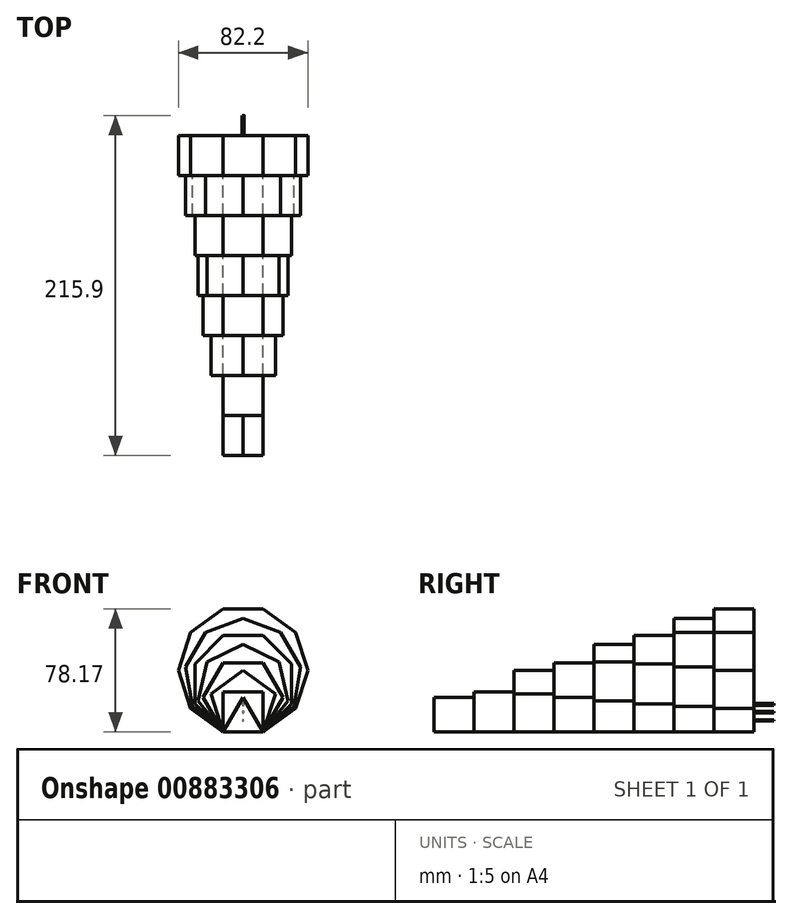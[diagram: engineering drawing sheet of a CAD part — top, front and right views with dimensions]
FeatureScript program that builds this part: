
annotation { "Feature Type Name" : "Feature", "Feature Type Description" : "" }
export const myFeature = defineFeature(function(context is Context, id is Id, definition is map)
    precondition{}
    {
        {
            var Q0;
            Q0=qCreatedBy(makeId("Front.planeOp"),FACE);
            var sketch = newSketch(context, id + "F0", { "sketchPlane" : qUnion([Q0])});
            skCircle(sketch, "E0.cCircle", {"center": v(0, 0) * mm, "radius": 14.66 * mm, "construction": true});
            skLineSegment(sketch, "E0.0", {"start": v(12.7, -7.33) * mm, "end": v(-12.7, -7.33) * mm});
            skLineSegment(sketch, "E0.1", {"start": v(-12.7, -7.33) * mm, "end": v(0, 14.66) * mm});
            skLineSegment(sketch, "E0.2", {"start": v(0, 14.66) * mm, "end": v(12.7, -7.33) * mm});
            skSolve(sketch);
        }
        {
            var Q0;
            Q0=makeQuery(id+"F0.imprint","IMPRINT",FACE,{"disambiguationData":[TD([[makeQuery(id+"F0.imprint","IMPRINT",EDGE,{"derivedFrom":sQuery(id+"F0.wireOp",EDGE,"E0.0")}),-1.0]])]});
            var Q1;
            Q1 = qSketchRegion(id + "F0", true);
            extrude(context, id + "F1", {"entities" : qUnion([Q0, Q1]), "depth" : 203.2 * mm, "offsetDistance" : 25.4 * mm});
        }
        {
            var Q0;
            Q0=qCreatedBy(makeId("Front.planeOp"),FACE);
            var sketch = newSketch(context, id + "F2", { "sketchPlane" : qUnion([Q0])});
            skCircle(sketch, "E1.cCircle", {"center": v(0, 5.37) * mm, "radius": 17.96 * mm, "construction": true});
            skLineSegment(sketch, "E1.0", {"start": v(12.7, -7.33) * mm, "end": v(-12.7, -7.33) * mm});
            skLineSegment(sketch, "E1.1", {"start": v(-12.7, -7.33) * mm, "end": v(-12.7, 18.07) * mm});
            skLineSegment(sketch, "E1.2", {"start": v(-12.7, 18.07) * mm, "end": v(12.7, 18.07) * mm});
            skLineSegment(sketch, "E1.3", {"start": v(12.7, 18.07) * mm, "end": v(12.7, -7.33) * mm});
            skSolve(sketch);
        }
        {
            var Q0;
            Q0 = qSketchRegion(id + "F2", true);
            extrude(context, id + "F3", {"entities" : qUnion([Q0]), "operationType" : NewBodyOperationType.ADD, "depth" : 177.8 * mm, "offsetDistance" : 25.4 * mm});
        }
        {
            var Q0;
            Q0=qCreatedBy(makeId("Front.planeOp"),FACE);
            var sketch = newSketch(context, id + "F4", { "sketchPlane" : qUnion([Q0])});
            skCircle(sketch, "E2.cCircle", {"center": v(0, 10.15) * mm, "radius": 21.6 * mm, "construction": true});
            skLineSegment(sketch, "E2.0", {"start": v(12.7, -7.33) * mm, "end": v(-12.7, -7.33) * mm});
            skLineSegment(sketch, "E2.1", {"start": v(-12.7, -7.33) * mm, "end": v(-20.55, 16.82) * mm});
            skLineSegment(sketch, "E2.2", {"start": v(-20.55, 16.82) * mm, "end": v(0, 31.75) * mm});
            skLineSegment(sketch, "E2.3", {"start": v(0, 31.75) * mm, "end": v(20.55, 16.82) * mm});
            skLineSegment(sketch, "E2.4", {"start": v(20.55, 16.82) * mm, "end": v(12.7, -7.33) * mm});
            skSolve(sketch);
        }
        {
            var Q0;
            Q0 = qSketchRegion(id + "F4", true);
            extrude(context, id + "F5", {"entities" : qUnion([Q0]), "operationType" : NewBodyOperationType.ADD, "depth" : 152.4 * mm, "offsetDistance" : 25.4 * mm});
        }
        {
            var Q0;
            Q0=qCreatedBy(makeId("Front.planeOp"),FACE);
            var sketch = newSketch(context, id + "F6", { "sketchPlane" : qUnion([Q0])});
            skCircle(sketch, "E3.cCircle", {"center": v(0, 14.66) * mm, "radius": 25.4 * mm, "construction": true});
            skLineSegment(sketch, "E3.0", {"start": v(12.7, -7.33) * mm, "end": v(-12.7, -7.33) * mm});
            skLineSegment(sketch, "E3.1", {"start": v(-12.7, -7.33) * mm, "end": v(-25.4, 14.66) * mm});
            skLineSegment(sketch, "E3.2", {"start": v(-25.4, 14.66) * mm, "end": v(-12.7, 36.66) * mm});
            skLineSegment(sketch, "E3.3", {"start": v(-12.7, 36.66) * mm, "end": v(12.7, 36.66) * mm});
            skLineSegment(sketch, "E3.4", {"start": v(12.7, 36.66) * mm, "end": v(25.4, 14.66) * mm});
            skLineSegment(sketch, "E3.5", {"start": v(25.4, 14.66) * mm, "end": v(12.7, -7.33) * mm});
            skSolve(sketch);
        }
        {
            var Q0;
            Q0 = qSketchRegion(id + "F6", true);
            extrude(context, id + "F7", {"entities" : qUnion([Q0]), "operationType" : NewBodyOperationType.ADD, "depth" : 127 * mm, "offsetDistance" : 25.4 * mm});
        }
        {
            var Q0;
            Q0=qCreatedBy(makeId("Front.planeOp"),FACE);
            var sketch = newSketch(context, id + "F8", { "sketchPlane" : qUnion([Q0])});
            skCircle(sketch, "E4.cCircle", {"center": v(0, 19.04) * mm, "radius": 29.27 * mm, "construction": true});
            skLineSegment(sketch, "E4.0", {"start": v(12.7, -7.33) * mm, "end": v(-12.7, -7.33) * mm});
            skLineSegment(sketch, "E4.1", {"start": v(-12.7, -7.33) * mm, "end": v(-28.54, 12.53) * mm});
            skLineSegment(sketch, "E4.2", {"start": v(-28.54, 12.53) * mm, "end": v(-22.88, 37.29) * mm});
            skLineSegment(sketch, "E4.3", {"start": v(-22.88, 37.29) * mm, "end": v(0, 48.3) * mm});
            skLineSegment(sketch, "E4.4", {"start": v(0, 48.3) * mm, "end": v(22.88, 37.29) * mm});
            skLineSegment(sketch, "E4.5", {"start": v(22.88, 37.29) * mm, "end": v(28.54, 12.53) * mm});
            skLineSegment(sketch, "E4.6", {"start": v(28.54, 12.53) * mm, "end": v(12.7, -7.33) * mm});
            skSolve(sketch);
        }
        {
            var Q0;
            Q0=makeQuery(id+"F8.imprint","IMPRINT",FACE,{"disambiguationData":[TD([[makeQuery(id+"F8.imprint","IMPRINT",EDGE,{"derivedFrom":sQuery(id+"F8.wireOp",EDGE,"E4.0")}),-1.0]])]});
            var Q1;
            Q1 = qSketchRegion(id + "F8", true);
            extrude(context, id + "F9", {"entities" : qUnion([Q0, Q1]), "operationType" : NewBodyOperationType.ADD, "depth" : 101.6 * mm, "offsetDistance" : 25.4 * mm});
        }
        {
            var Q0;
            Q0=qCreatedBy(makeId("Front.planeOp"),FACE);
            var sketch = newSketch(context, id + "F10", { "sketchPlane" : qUnion([Q0])});
            skCircle(sketch, "E5.cCircle", {"center": v(0, 23.33) * mm, "radius": 33.19 * mm, "construction": true});
            skLineSegment(sketch, "E5.0", {"start": v(12.7, -7.33) * mm, "end": v(-12.7, -7.33) * mm});
            skLineSegment(sketch, "E5.1", {"start": v(-12.7, -7.33) * mm, "end": v(-30.66, 10.63) * mm});
            skLineSegment(sketch, "E5.2", {"start": v(-30.66, 10.63) * mm, "end": v(-30.66, 36.03) * mm});
            skLineSegment(sketch, "E5.3", {"start": v(-30.66, 36.03) * mm, "end": v(-12.7, 53.99) * mm});
            skLineSegment(sketch, "E5.4", {"start": v(-12.7, 53.99) * mm, "end": v(12.7, 53.99) * mm});
            skLineSegment(sketch, "E5.5", {"start": v(12.7, 53.99) * mm, "end": v(30.66, 36.03) * mm});
            skLineSegment(sketch, "E5.6", {"start": v(30.66, 36.03) * mm, "end": v(30.66, 10.63) * mm});
            skLineSegment(sketch, "E5.7", {"start": v(30.66, 10.63) * mm, "end": v(12.7, -7.33) * mm});
            skSolve(sketch);
        }
        {
            var Q0;
            Q0 = qSketchRegion(id + "F10", true);
            extrude(context, id + "F11", {"entities" : qUnion([Q0]), "operationType" : NewBodyOperationType.ADD, "depth" : 76.2 * mm, "offsetDistance" : 25.4 * mm});
        }
        {
            var Q0;
            Q0=qCreatedBy(makeId("Front.planeOp"),FACE);
            var sketch = newSketch(context, id + "F12", { "sketchPlane" : qUnion([Q0])});
            skCircle(sketch, "E6.cCircle", {"center": v(0, 27.56) * mm, "radius": 37.13 * mm, "construction": true});
            skLineSegment(sketch, "E6.0", {"start": v(12.7, -7.33) * mm, "end": v(-12.7, -7.33) * mm});
            skLineSegment(sketch, "E6.1", {"start": v(-12.7, -7.33) * mm, "end": v(-32.16, 9) * mm});
            skLineSegment(sketch, "E6.2", {"start": v(-32.16, 9) * mm, "end": v(-36.57, 34) * mm});
            skLineSegment(sketch, "E6.3", {"start": v(-36.57, 34) * mm, "end": v(-23.87, 56) * mm});
            skLineSegment(sketch, "E6.4", {"start": v(-23.87, 56) * mm, "end": v(0, 64.7) * mm});
            skLineSegment(sketch, "E6.5", {"start": v(0, 64.7) * mm, "end": v(23.87, 56) * mm});
            skLineSegment(sketch, "E6.6", {"start": v(23.87, 56) * mm, "end": v(36.57, 34) * mm});
            skLineSegment(sketch, "E6.7", {"start": v(36.57, 34) * mm, "end": v(32.16, 9) * mm});
            skLineSegment(sketch, "E6.8", {"start": v(32.16, 9) * mm, "end": v(12.7, -7.33) * mm});
            skSolve(sketch);
        }
        {
            var Q0;
            Q0 = qSketchRegion(id + "F12", true);
            extrude(context, id + "F13", {"entities" : qUnion([Q0]), "operationType" : NewBodyOperationType.ADD, "depth" : 50.8 * mm, "offsetDistance" : 25.4 * mm});
        }
        {
            var Q0;
            Q0=qCreatedBy(makeId("Front.planeOp"),FACE);
            var sketch = newSketch(context, id + "F14", { "sketchPlane" : qUnion([Q0])});
            skCircle(sketch, "E7.cCircle", {"center": v(0, 31.75) * mm, "radius": 41.1 * mm, "construction": true});
            skLineSegment(sketch, "E7.0", {"start": v(12.7, -7.33) * mm, "end": v(-12.7, -7.33) * mm});
            skLineSegment(sketch, "E7.1", {"start": v(-12.7, -7.33) * mm, "end": v(-33.25, 7.6) * mm});
            skLineSegment(sketch, "E7.2", {"start": v(-33.25, 7.6) * mm, "end": v(-41.1, 31.75) * mm});
            skLineSegment(sketch, "E7.3", {"start": v(-41.1, 31.75) * mm, "end": v(-33.25, 55.91) * mm});
            skLineSegment(sketch, "E7.4", {"start": v(-33.25, 55.91) * mm, "end": v(-12.7, 70.84) * mm});
            skLineSegment(sketch, "E7.5", {"start": v(-12.7, 70.84) * mm, "end": v(12.7, 70.84) * mm});
            skLineSegment(sketch, "E7.6", {"start": v(12.7, 70.84) * mm, "end": v(33.25, 55.91) * mm});
            skLineSegment(sketch, "E7.7", {"start": v(33.25, 55.91) * mm, "end": v(41.1, 31.75) * mm});
            skLineSegment(sketch, "E7.8", {"start": v(41.1, 31.75) * mm, "end": v(33.25, 7.6) * mm});
            skLineSegment(sketch, "E7.9", {"start": v(33.25, 7.6) * mm, "end": v(12.7, -7.33) * mm});
            skSolve(sketch);
        }
        {
            var Q0;
            Q0 = qSketchRegion(id + "F14", true);
            extrude(context, id + "F15", {"entities" : qUnion([Q0]), "operationType" : NewBodyOperationType.ADD, "depth" : 25.4 * mm, "offsetDistance" : 25.4 * mm});
        }
        {
            var Q0;
            Q0=makeQuery(id+"F3.opExtrude","CAP_FACE",FACE,{"disambiguationData":[OSD([sQuery(id+"F2.wireOp",EDGE,"E1.0"),sQuery(id+"F2.wireOp",EDGE,"E1.1"),sQuery(id+"F2.wireOp",EDGE,"E1.2"),sQuery(id+"F2.wireOp",EDGE,"E1.3")])],"isStart":false});
            var sketch = newSketch(context, id + "F16", { "sketchPlane" : qUnion([Q0])});
            skLineSegment(sketch, "E8", {"start": v(-12.7, 18.07) * mm, "end": v(12.7, -7.33) * mm, "construction": true});
            skLineSegment(sketch, "E9", {"start": v(12.7, -7.33) * mm, "end": v(12.7, 18.07) * mm, "construction": true});
            skLineSegment(sketch, "E10", {"start": v(12.7, 18.07) * mm, "end": v(-12.7, -7.33) * mm, "construction": true});
            skPoint(sketch, "E11", {"position": v(0, 5.37) * mm});
            skCircle(sketch, "E12", {"center": v(0, 5.37) * mm, "radius": 0.5 * mm});
            skSolve(sketch);
        }
        {
            var Q0;
            Q0 = qSketchRegion(id + "F16", true);
            extrude(context, id + "F17", {"entities" : qUnion([Q0]), "operationType" : NewBodyOperationType.ADD, "oppositeDirection" : true, "depth" : 190.5 * mm, "offsetDistance" : 25.4 * mm});
        }
        {
            var Q0;
            Q0=makeQuery(id+"F1.opExtrude","CAP_FACE",FACE,{"disambiguationData":[OSD([sQuery(id+"F0.wireOp",EDGE,"E0.0"),sQuery(id+"F0.wireOp",EDGE,"E0.1"),sQuery(id+"F0.wireOp",EDGE,"E0.2")])],"isStart":false});
            var sketch = newSketch(context, id + "F18", { "sketchPlane" : qUnion([Q0])});
            skCircle(sketch, "E13", {"center": v(0, 0) * mm, "radius": 0.38 * mm});
            skSolve(sketch);
        }
        {
            var Q0;
            Q0 = qSketchRegion(id + "F18", true);
            extrude(context, id + "F19", {"entities" : qUnion([Q0]), "operationType" : NewBodyOperationType.ADD, "oppositeDirection" : true, "depth" : 215.9 * mm, "offsetDistance" : 25.4 * mm});
        }
        {
            var Q0;
            Q0=makeQuery(id+"F5.opExtrude","CAP_FACE",FACE,{"disambiguationData":[OSD([sQuery(id+"F4.wireOp",EDGE,"E2.0"),sQuery(id+"F4.wireOp",EDGE,"E2.1"),sQuery(id+"F4.wireOp",EDGE,"E2.2"),sQuery(id+"F4.wireOp",EDGE,"E2.3"),sQuery(id+"F4.wireOp",EDGE,"E2.4")])],"isStart":false});
            var sketch = newSketch(context, id + "F20", { "sketchPlane" : qUnion([Q0])});
            skLineSegment(sketch, "E14", {"start": v(0, 31.75) * mm, "end": v(0, -3.52) * mm, "construction": true});
            skLineSegment(sketch, "E15", {"start": v(20.55, 16.82) * mm, "end": v(-20.17, 3.6) * mm, "construction": true});
            skPoint(sketch, "E16", {"position": v(0, 10.15) * mm});
            skCircle(sketch, "E17", {"center": v(0, 10.15) * mm, "radius": 0.64 * mm});
            skSolve(sketch);
        }
        {
            var Q0;
            Q0 = qSketchRegion(id + "F20", true);
            extrude(context, id + "F21", {"entities" : qUnion([Q0]), "operationType" : NewBodyOperationType.ADD, "oppositeDirection" : true, "depth" : 165.1 * mm, "offsetDistance" : 25.4 * mm});
        }
    });
